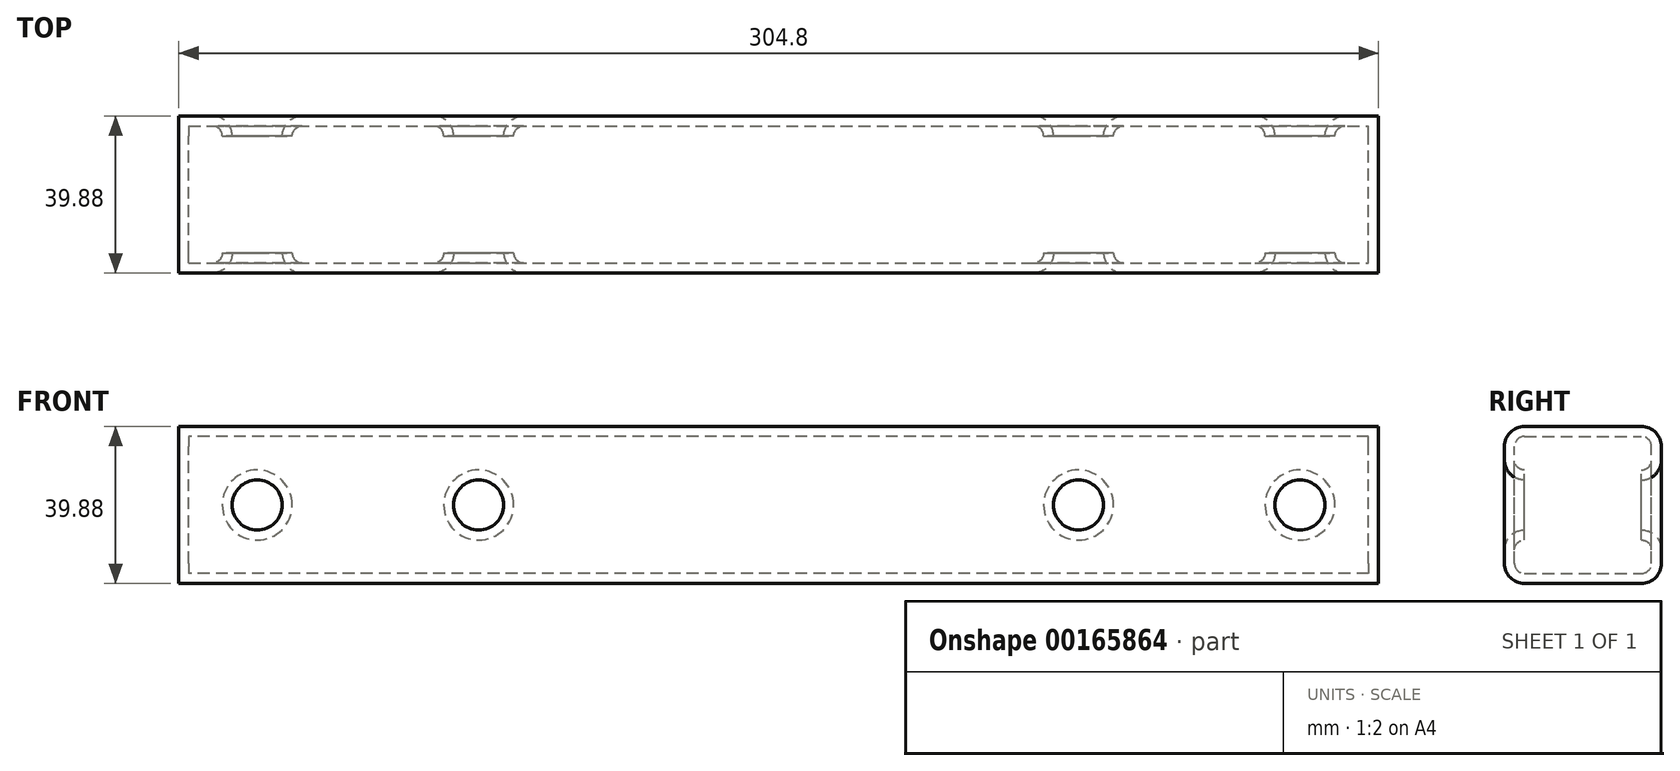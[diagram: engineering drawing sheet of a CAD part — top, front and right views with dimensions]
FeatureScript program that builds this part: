
annotation { "Feature Type Name" : "Feature", "Feature Type Description" : "" }
export const myFeature = defineFeature(function(context is Context, id is Id, definition is map)
    precondition{}
    {
        {
            var Q0;
            Q0=qCreatedBy(makeId("Front.planeOp"),FACE);
            var sketch = newSketch(context, id + "F0", { "sketchPlane" : qUnion([Q0])});
            skLineSegment(sketch, "E0.bottom", {"start": v(152.4, -19.94) * mm, "end": v(-152.4, -19.94) * mm});
            skLineSegment(sketch, "E0.top", {"start": v(152.4, 19.94) * mm, "end": v(-152.4, 19.94) * mm});
            skLineSegment(sketch, "E0.left", {"start": v(152.4, -19.94) * mm, "end": v(152.4, 19.94) * mm});
            skLineSegment(sketch, "E0.right", {"start": v(-152.4, -19.94) * mm, "end": v(-152.4, 19.94) * mm});
            skPoint(sketch, "E0.middle", {"position": v(0, 0) * mm});
            skLineSegment(sketch, "E1", {"start": v(-152.4, 19.94) * mm, "end": v(-112.52, 19.94) * mm});
            skLineSegment(sketch, "E2", {"start": v(-112.52, -19.94) * mm, "end": v(-152.4, -19.94) * mm});
            skPoint(sketch, "E3.startSnap0", {"position": v(-132.46, 19.94) * mm});
            skCircle(sketch, "E4", {"center": v(-132.46, 0) * mm, "radius": 6.35 * mm});
            skCircle(sketch, "E5.MirrorC", {"center": v(132.46, 0) * mm, "radius": 6.35 * mm});
            skLineSegment(sketch, "E6", {"start": v(0, 19.94) * mm, "end": v(-76.2, 19.94) * mm});
            skLineSegment(sketch, "E7", {"start": v(0, 19.94) * mm, "end": v(76.2, 19.94) * mm});
            skCircle(sketch, "E8", {"center": v(-76.2, 0) * mm, "radius": 6.35 * mm});
            skCircle(sketch, "E9.MirrorC", {"center": v(76.2, 0) * mm, "radius": 6.35 * mm});
            skSolve(sketch);
        }
        {
            var Q0;
            Q0 = qSketchRegion(id + "F0", true);
            extrude(context, id + "F1", {"entities" : qUnion([Q0]), "depth" : 39.88 * mm});
        }
        {
            var Q0;
            Q0=makeQuery(id+"F1.opExtrude","CAP_EDGE",EDGE,{"disambiguationData":[OSD([sQuery(id+"F0.wireOp",EDGE,"E4")])],"isStart":false});
            var Q1;
            Q1=makeQuery(id+"F1.opExtrude","CAP_EDGE",EDGE,{"disambiguationData":[OSD([sQuery(id+"F0.wireOp",EDGE,"E8")])],"isStart":false});
            var Q2;
            Q2=makeQuery(id+"F1.opExtrude","CAP_EDGE",EDGE,{"disambiguationData":[OSD([sQuery(id+"F0.wireOp",EDGE,"E9.MirrorC")])],"isStart":false});
            fillet(context, id + "F2", {"entities" : qUnion([Q0, Q1, Q2]), "radius" : 5.08 * mm, "tangentPropagation" : true, "allowEdgeOverflow" : false});
        }
        {
            var Q0;
            Q0=makeQuery(id+"F1.opExtrude","CAP_EDGE",EDGE,{"disambiguationData":[OSD([sQuery(id+"F0.wireOp",EDGE,"E5.MirrorC")])],"isStart":false});
            var Q1;
            Q1=makeQuery(id+"F1.opExtrude","CAP_EDGE",EDGE,{"disambiguationData":[OSD([sQuery(id+"F0.wireOp",EDGE,"E5.MirrorC")])],"isStart":true});
            var Q2;
            Q2=makeQuery(id+"F1.opExtrude","CAP_EDGE",EDGE,{"disambiguationData":[OSD([sQuery(id+"F0.wireOp",EDGE,"E9.MirrorC")])],"isStart":true});
            var Q3;
            Q3=makeQuery(id+"F1.opExtrude","CAP_EDGE",EDGE,{"disambiguationData":[OSD([sQuery(id+"F0.wireOp",EDGE,"E8")])],"isStart":true});
            var Q4;
            Q4=makeQuery(id+"F1.opExtrude","CAP_EDGE",EDGE,{"disambiguationData":[OSD([sQuery(id+"F0.wireOp",EDGE,"E4")])],"isStart":true});
            var Q5;
            Q5=makeQuery(id+"F1.opExtrude","CAP_EDGE",EDGE,{"disambiguationData":[OSD([sQuery(id+"F0.wireOp",EDGE,"E0.bottom"),sQuery(id+"F0.wireOp",EDGE,"E2")])],"isStart":true});
            var Q6;
            Q6=makeQuery(id+"F1.opExtrude","CAP_EDGE",EDGE,{"disambiguationData":[OSD([sQuery(id+"F0.wireOp",EDGE,"E0.top"),sQuery(id+"F0.wireOp",EDGE,"E1"),sQuery(id+"F0.wireOp",EDGE,"E6"),sQuery(id+"F0.wireOp",EDGE,"E7")])],"isStart":true});
            var Q7;
            Q7=makeQuery(id+"F1.opExtrude","CAP_EDGE",EDGE,{"disambiguationData":[OSD([sQuery(id+"F0.wireOp",EDGE,"E0.top"),sQuery(id+"F0.wireOp",EDGE,"E1"),sQuery(id+"F0.wireOp",EDGE,"E6"),sQuery(id+"F0.wireOp",EDGE,"E7")])],"isStart":false});
            var Q8;
            Q8=makeQuery(id+"F1.opExtrude","CAP_EDGE",EDGE,{"disambiguationData":[OSD([sQuery(id+"F0.wireOp",EDGE,"E0.bottom"),sQuery(id+"F0.wireOp",EDGE,"E2")])],"isStart":false});
            fillet(context, id + "F3", {"entities" : qUnion([Q0, Q1, Q2, Q3, Q4, Q5, Q6, Q7, Q8]), "radius" : 5.08 * mm, "tangentPropagation" : true, "allowEdgeOverflow" : false});
        }
        {
            var Q0;
            Q0=makeQuery(id+"F1.opExtrude","SWEPT_FACE",FACE,{"disambiguationData":[OSD([sQuery(id+"F0.wireOp",EDGE,"E9.MirrorC")])]});
            var Q1;
            Q1=makeQuery(id+"F1.opExtrude","SWEPT_FACE",FACE,{"disambiguationData":[OSD([sQuery(id+"F0.wireOp",EDGE,"E5.MirrorC")])]});
            var Q2;
            Q2=makeQuery(id+"F1.opExtrude","SWEPT_FACE",FACE,{"disambiguationData":[OSD([sQuery(id+"F0.wireOp",EDGE,"E8")])]});
            var Q3;
            Q3=makeQuery(id+"F1.opExtrude","SWEPT_FACE",FACE,{"disambiguationData":[OSD([sQuery(id+"F0.wireOp",EDGE,"E4")])]});
            shell(context, id + "F4", {"entities" : qUnion([Q0, Q1, Q2, Q3]), "thickness" : 2.54 * mm});
        }
    });
